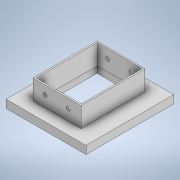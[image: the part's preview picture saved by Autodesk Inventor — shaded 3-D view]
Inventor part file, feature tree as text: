
AUTODESK INVENTOR PART (.ipt)
format: ipt  version: 2021 (Build 250183000, 183)  size: 134,144 bytes
history: native  units: mm
features: extrude x4, sketch x4
ambient origin geometry x8: Origin, YZ Plane, XZ Plane, XY Plane, X Axis, Y Axis, Z Axis, Center Point
bodies: Solid1 (feature_tree)
feature tree (8):
  extrude  "Extrusion1"  Depth=1000.0mm
  extrude  "Extrusion2"  Depth=800.0mm
  extrude  "Extrusion3"  Depth=150.0mm
  extrude  "Extrusion4"  Depth=250.0mm TaperAngle=0.0deg
  sketch  "Sketch1"  dims[d0=1100.0mm d1=1000.0mm]
  sketch  "Sketch2"  dims[d2=100.0mm d3=0.0mm d4=800.0mm]
  sketch  "Sketch3"  dims[d5=600.0mm d6=150.0mm]
  sketch  "Sketch4"  dims[d7=100.0mm d8=0.0mm d9=250.0mm d10=0.0mm d11=50.0mm d12=50.0mm d13=2500.0mm d14=0.0mm]
